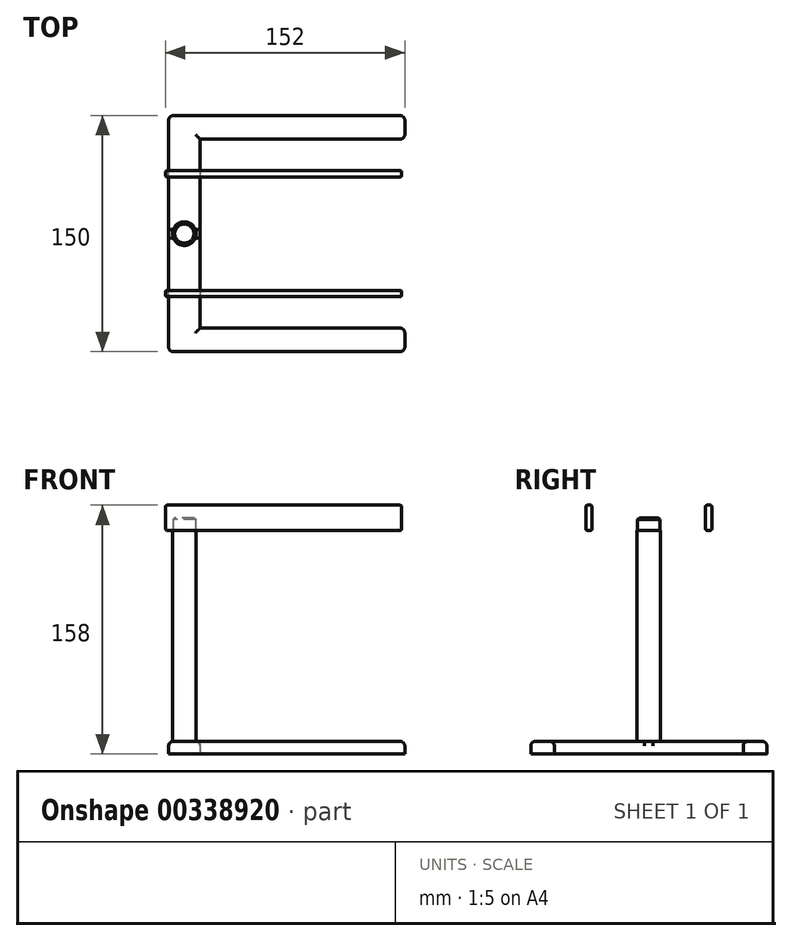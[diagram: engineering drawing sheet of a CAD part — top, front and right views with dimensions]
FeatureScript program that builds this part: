
annotation { "Feature Type Name" : "Feature", "Feature Type Description" : "" }
export const myFeature = defineFeature(function(context is Context, id is Id, definition is map)
    precondition{}
    {
        {
            assignVariable(context, id + "F0", {"name" : "base_height", "anyValue" : 8 * mm});
        }
        {
            assignVariable(context, id + "F1", {"name" : "rail_height", "anyValue" : 150 * mm});
        }
        {
            var Q0;
            Q0=qCreatedBy(makeId("Top.planeOp"),FACE);
            var sketch = newSketch(context, id + "F2", { "sketchPlane" : qUnion([Q0])});
            skLineSegment(sketch, "E0.bottom", {"start": v(75, -75) * mm, "end": v(-75, -75) * mm});
            skLineSegment(sketch, "E0.top", {"start": v(75, 75) * mm, "end": v(-75, 75) * mm});
            skLineSegment(sketch, "E0.left", {"start": v(75, -75) * mm, "end": v(75, -60) * mm});
            skLineSegment(sketch, "E0.right", {"start": v(-75, -75) * mm, "end": v(-75, 75) * mm});
            skPoint(sketch, "E0.middle", {"position": v(0, 0) * mm});
            skLineSegment(sketch, "E1.bottom", {"start": v(75, 60) * mm, "end": v(-55, 60) * mm});
            skLineSegment(sketch, "E1.top", {"start": v(75, -60) * mm, "end": v(-55, -60) * mm});
            skLineSegment(sketch, "E1.right", {"start": v(-55, 60) * mm, "end": v(-55, -60) * mm});
            skLineSegment(sketch, "E2.trimOffspring", {"start": v(75, 60) * mm, "end": v(75, 75) * mm});
            skCircle(sketch, "E3", {"center": v(-65, 0) * mm, "radius": 7.5 * mm});
            skPoint(sketch, "E3.centerSnap0", {"position": v(-75, 0) * mm});
            skSolve(sketch);
        }
        {
            var Q0;
            Q0=makeQuery(id+"F2.imprint","IMPRINT",FACE,{"disambiguationData":[TD([[makeQuery(id+"F2.imprint","IMPRINT",EDGE,{"derivedFrom":sQuery(id+"F2.wireOp",EDGE,"E0.bottom")}),-1.0]])]});
            var Q1;
            Q1=makeQuery(id+"F2.imprint","IMPRINT",FACE,{"disambiguationData":[TD([[makeQuery(id+"F2.imprint","IMPRINT",EDGE,{"derivedFrom":sQuery(id+"F2.wireOp",EDGE,"E3")}),1.0]])]});
            extrude(context, id + "F3", {"entities" : qUnion([Q0, Q1]), "depth" : getVariable(context, 'base_height')});
        }
        {
            var Q0;
            Q0=makeQuery(id+"F2.imprint","IMPRINT",FACE,{"disambiguationData":[TD([[makeQuery(id+"F2.imprint","IMPRINT",EDGE,{"derivedFrom":sQuery(id+"F2.wireOp",EDGE,"E3")}),1.0]])]});
            extrude(context, id + "F4", {"entities" : qUnion([Q0]), "operationType" : NewBodyOperationType.ADD, "depth" : getVariable(context, 'rail_height') - getVariable(context, 'base_height')});
        }
        {
            var Q0;
            Q0=makeQuery(id+"F4.opExtrude","CAP_FACE",FACE,{"disambiguationData":[OSD([sQuery(id+"F2.wireOp",EDGE,"E3")])],"isStart":false});
            var sketch = newSketch(context, id + "F5", { "sketchPlane" : qUnion([Q0])});
            skCircle(sketch, "E4.0", {"center": v(-65, 0) * mm, "radius": 7.1 * mm});
            skSolve(sketch);
        }
        {
            var Q0;
            Q0=makeQuery(id+"F5.imprint","IMPRINT",FACE,{"disambiguationData":[TD([[makeQuery(id+"F5.imprint","IMPRINT",EDGE,{"derivedFrom":sQuery(id+"F5.wireOp",EDGE,"E4.0")}),1.0]])]});
            extrude(context, id + "F6", {"entities" : qUnion([Q0]), "operationType" : NewBodyOperationType.ADD, "depth" : getVariable(context, 'base_height')});
        }
        {
            var Q0;
            Q0=makeQuery(id+"F6.opExtrude","CAP_EDGE",EDGE,{"disambiguationData":[OSD([sQuery(id+"F5.wireOp",EDGE,"E4.0")])],"isStart":false});
            chamfer(context, id + "F7", {"entities" : qUnion([Q0]), "width" : 1 * mm, "tangentPropagation" : true});
        }
        {
            var Q0;
            Q0=makeQuery(id+"F3.opExtrude","CAP_EDGE",EDGE,{"disambiguationData":[OSD([sQuery(id+"F2.wireOp",EDGE,"E1.bottom")])],"isStart":false});
            var Q1;
            Q1=makeQuery(id+"F3.opExtrude","CAP_EDGE",EDGE,{"disambiguationData":[OSD([sQuery(id+"F2.wireOp",EDGE,"E0.top")])],"isStart":false});
            var Q2;
            Q2=makeQuery(id+"F3.opExtrude","CAP_EDGE",EDGE,{"disambiguationData":[OSD([sQuery(id+"F2.wireOp",EDGE,"E0.right")])],"isStart":false});
            var Q3;
            Q3=makeQuery(id+"F3.opExtrude","CAP_EDGE",EDGE,{"disambiguationData":[OSD([sQuery(id+"F2.wireOp",EDGE,"E2.trimOffspring")])],"isStart":false});
            var Q4;
            Q4=makeQuery(id+"F3.opExtrude","CAP_EDGE",EDGE,{"disambiguationData":[OSD([sQuery(id+"F2.wireOp",EDGE,"E0.left")])],"isStart":false});
            var Q5;
            Q5=makeQuery(id+"F3.opExtrude","CAP_EDGE",EDGE,{"disambiguationData":[OSD([sQuery(id+"F2.wireOp",EDGE,"E1.top")])],"isStart":false});
            var Q6;
            Q6=makeQuery(id+"F3.opExtrude","CAP_EDGE",EDGE,{"disambiguationData":[OSD([sQuery(id+"F2.wireOp",EDGE,"E0.bottom")])],"isStart":false});
            var Q7;
            Q7=makeQuery(id+"F3.opExtrude","CAP_EDGE",EDGE,{"disambiguationData":[OSD([sQuery(id+"F2.wireOp",EDGE,"E1.right")])],"isStart":false});
            var Q8;
            Q8=makeQuery(id+"F3.opExtrude","SWEPT_EDGE",EDGE,{"disambiguationData":[OSD([sQuery(id+"F2.wireOp",EDGE,"E1.bottom"),sQuery(id+"F2.wireOp",EDGE,"E2.trimOffspring")])]});
            var Q9;
            Q9=makeQuery(id+"F3.opExtrude","SWEPT_EDGE",EDGE,{"disambiguationData":[OSD([sQuery(id+"F2.wireOp",EDGE,"E0.top"),sQuery(id+"F2.wireOp",EDGE,"E2.trimOffspring")])]});
            var Q10;
            Q10=makeQuery(id+"F3.opExtrude","SWEPT_EDGE",EDGE,{"disambiguationData":[OSD([sQuery(id+"F2.wireOp",EDGE,"E0.left"),sQuery(id+"F2.wireOp",EDGE,"E1.top")])]});
            var Q11;
            Q11=makeQuery(id+"F3.opExtrude","SWEPT_EDGE",EDGE,{"disambiguationData":[OSD([sQuery(id+"F2.wireOp",EDGE,"E0.bottom"),sQuery(id+"F2.wireOp",EDGE,"E0.left")])]});
            var Q12;
            Q12=makeQuery(id+"F3.opExtrude","SWEPT_EDGE",EDGE,{"disambiguationData":[OSD([sQuery(id+"F2.wireOp",EDGE,"E0.bottom"),sQuery(id+"F2.wireOp",EDGE,"E0.right")])]});
            var Q13;
            Q13=makeQuery(id+"F3.opExtrude","SWEPT_EDGE",EDGE,{"disambiguationData":[OSD([sQuery(id+"F2.wireOp",EDGE,"E0.top"),sQuery(id+"F2.wireOp",EDGE,"E0.right")])]});
            fillet(context, id + "F8", {"entities" : qUnion([Q0, Q1, Q2, Q3, Q4, Q5, Q6, Q7, Q8, Q9, Q10, Q11, Q12, Q13]), "radius" : 3 * mm, "tangentPropagation" : true, "allowEdgeOverflow" : false});
        }
        {
            var Q0;
            Q0=makeQuery(id+"F4.opExtrude","CAP_FACE",FACE,{"disambiguationData":[OSD([sQuery(id+"F2.wireOp",EDGE,"E3")])],"isStart":false});
            var sketch = newSketch(context, id + "F9", { "sketchPlane" : qUnion([Q0])});
            skLineSegment(sketch, "E5.bottom", {"start": v(-77, 40) * mm, "end": v(73, 40) * mm});
            skLineSegment(sketch, "E5.top", {"start": v(-77, -40) * mm, "end": v(73, -40) * mm});
            skLineSegment(sketch, "E5.left", {"start": v(-77, 40) * mm, "end": v(-77, -40) * mm});
            skLineSegment(sketch, "E5.right", {"start": v(73, 40) * mm, "end": v(73, -40) * mm});
            skCircle(sketch, "E6.0", {"center": v(-65, 0) * mm, "radius": 7.5 * mm});
            skCircle(sketch, "E7", {"center": v(48, 0) * mm, "radius": 22.5 * mm});
            skCircle(sketch, "E8", {"center": v(0, 0) * mm, "radius": 17.5 * mm});
            skCircle(sketch, "E9", {"center": v(-38, 0) * mm, "radius": 12.5 * mm});
            skLineSegment(sketch, "E10.top", {"start": v(-77, 36) * mm, "end": v(73, 36) * mm});
            skLineSegment(sketch, "E10.left", {"start": v(-77, 40) * mm, "end": v(-77, 36) * mm});
            skLineSegment(sketch, "E10.right", {"start": v(73, 40) * mm, "end": v(73, 36) * mm});
            skLineSegment(sketch, "E11.top", {"start": v(-77, -36) * mm, "end": v(73, -36) * mm});
            skLineSegment(sketch, "E11.left", {"start": v(-77, -40) * mm, "end": v(-77, -36) * mm});
            skLineSegment(sketch, "E11.right", {"start": v(73, -40) * mm, "end": v(73, -36) * mm});
            skSolve(sketch);
        }
        {
            var Q0;
            Q0=makeQuery(id+"F9.imprint","IMPRINT",FACE,{"disambiguationData":[TD([[makeQuery(id+"F9.imprint","IMPRINT",EDGE,{"derivedFrom":sQuery(id+"F9.wireOp",EDGE,"E5.left")}),1.0]])]});
            var Q1;
            Q1=makeQuery(id+"F9.imprint","IMPRINT",FACE,{"disambiguationData":[TD([[makeQuery(id+"F9.imprint","IMPRINT",EDGE,{"derivedFrom":sQuery(id+"F9.wireOp",EDGE,"E5.bottom")}),-1.0]])]});
            var Q2;
            Q2=makeQuery(id+"F9.imprint","IMPRINT",FACE,{"disambiguationData":[TD([[makeQuery(id+"F9.imprint","IMPRINT",EDGE,{"derivedFrom":sQuery(id+"F9.wireOp",EDGE,"E5.top")}),1.0]])]});
            var Q3;
            Q3=makeQuery(id+"F6.opExtrude","CAP_FACE",FACE,{"disambiguationData":[OSD([sQuery(id+"F5.wireOp",EDGE,"E4.0")])],"isStart":false});
            extrude(context, id + "F10", {"entities" : qUnion([Q0, Q1, Q2]), "endBound" : BoundingType.UP_TO_SURFACE, "endBoundEntityFace" : qUnion([Q3]), "depth" : 25 * mm});
        }
        {
            var Q0;
            Q0=makeQuery(id+"F9.imprint","IMPRINT",FACE,{"disambiguationData":[TD([[makeQuery(id+"F9.imprint","IMPRINT",EDGE,{"derivedFrom":sQuery(id+"F9.wireOp",EDGE,"E5.bottom")}),-1.0]])]});
            var Q1;
            Q1=makeQuery(id+"F9.imprint","IMPRINT",FACE,{"disambiguationData":[TD([[makeQuery(id+"F9.imprint","IMPRINT",EDGE,{"derivedFrom":sQuery(id+"F9.wireOp",EDGE,"E5.top")}),1.0]])]});
            extrude(context, id + "F11", {"entities" : qUnion([Q0, Q1]), "operationType" : NewBodyOperationType.ADD, "depth" : getVariable(context, 'base_height') * 2});
        }
        {
            var Q0;
            Q0=makeQuery(id+"F10.opExtrude","CAP_FACE",FACE,{"disambiguationData":[OSD([sQuery(id+"F9.wireOp",EDGE,"E5.left"),sQuery(id+"F9.wireOp",EDGE,"E5.right"),sQuery(id+"F9.wireOp",EDGE,"E6.0"),sQuery(id+"F9.wireOp",EDGE,"E7"),sQuery(id+"F9.wireOp",EDGE,"E8"),sQuery(id+"F9.wireOp",EDGE,"E9"),sQuery(id+"F9.wireOp",EDGE,"E5.bottom"),sQuery(id+"F9.wireOp",EDGE,"E10.left"),sQuery(id+"F9.wireOp",EDGE,"E10.right"),sQuery(id+"F9.wireOp",EDGE,"E5.top"),sQuery(id+"F9.wireOp",EDGE,"E11.left"),sQuery(id+"F9.wireOp",EDGE,"E11.right")])],"isStart":false});
            var Q1;
            Q1=makeQuery(id+"F10.opExtrude","CAP_FACE",FACE,{"disambiguationData":[OSD([sQuery(id+"F9.wireOp",EDGE,"E5.left"),sQuery(id+"F9.wireOp",EDGE,"E5.right"),sQuery(id+"F9.wireOp",EDGE,"E6.0"),sQuery(id+"F9.wireOp",EDGE,"E7"),sQuery(id+"F9.wireOp",EDGE,"E8"),sQuery(id+"F9.wireOp",EDGE,"E9"),sQuery(id+"F9.wireOp",EDGE,"E5.bottom"),sQuery(id+"F9.wireOp",EDGE,"E10.left"),sQuery(id+"F9.wireOp",EDGE,"E10.right"),sQuery(id+"F9.wireOp",EDGE,"E5.top"),sQuery(id+"F9.wireOp",EDGE,"E11.left"),sQuery(id+"F9.wireOp",EDGE,"E11.right")])],"isStart":true});
            var Q2;
            {var subQ0=sQuery(id+"F9.wireOp",EDGE,"E11.right");var subQ1=sQuery(id+"F9.wireOp",EDGE,"E10.right");Q2=makeQuery(id+"F11.boolean.opBoolean","MERGE",FACE,{"derivedFrom":[makeQuery(id+"F10.opExtrude","SWEPT_FACE",FACE,{"disambiguationData":[OSD([sQuery(id+"F9.wireOp",EDGE,"E5.right"),subQ1,subQ0])]}),makeQuery(id+"F11.opExtrude","SWEPT_FACE",FACE,{"disambiguationData":[OSD([subQ1])]}),makeQuery(id+"F11.opExtrude","SWEPT_FACE",FACE,{"disambiguationData":[OSD([subQ0])]})]});}
            var Q3;
            Q3=makeQuery(id+"F10.opExtrude","SWEPT_FACE",FACE,{"disambiguationData":[OSD([sQuery(id+"F9.wireOp",EDGE,"E5.top")])]});
            var Q4;
            {var subQ0=sQuery(id+"F9.wireOp",EDGE,"E11.left");var subQ1=sQuery(id+"F9.wireOp",EDGE,"E10.left");Q4=makeQuery(id+"F11.boolean.opBoolean","MERGE",FACE,{"derivedFrom":[makeQuery(id+"F10.opExtrude","SWEPT_FACE",FACE,{"disambiguationData":[OSD([sQuery(id+"F9.wireOp",EDGE,"E5.left"),subQ1,subQ0])]}),makeQuery(id+"F11.opExtrude","SWEPT_FACE",FACE,{"disambiguationData":[OSD([subQ1])]}),makeQuery(id+"F11.opExtrude","SWEPT_FACE",FACE,{"disambiguationData":[OSD([subQ0])]})]});}
            var Q5;
            Q5=makeQuery(id+"F10.opExtrude","SWEPT_FACE",FACE,{"disambiguationData":[OSD([sQuery(id+"F9.wireOp",EDGE,"E5.bottom")])]});
            var Q6;
            Q6=makeQuery(id+"F11.opExtrude","CAP_FACE",FACE,{"disambiguationData":[OSD([sQuery(id+"F9.wireOp",EDGE,"E5.top"),sQuery(id+"F9.wireOp",EDGE,"E11.top"),sQuery(id+"F9.wireOp",EDGE,"E11.left"),sQuery(id+"F9.wireOp",EDGE,"E11.right")])],"isStart":false});
            var Q7;
            Q7=makeQuery(id+"F11.opExtrude","CAP_FACE",FACE,{"disambiguationData":[OSD([sQuery(id+"F9.wireOp",EDGE,"E5.bottom"),sQuery(id+"F9.wireOp",EDGE,"E10.top"),sQuery(id+"F9.wireOp",EDGE,"E10.left"),sQuery(id+"F9.wireOp",EDGE,"E10.right")])],"isStart":false});
            fillet(context, id + "F12", {"entities" : qUnion([Q0, Q1, Q2, Q3, Q4, Q5, Q6, Q7]), "radius" : 1 * mm, "tangentPropagation" : true, "allowEdgeOverflow" : false});
        }
    });
